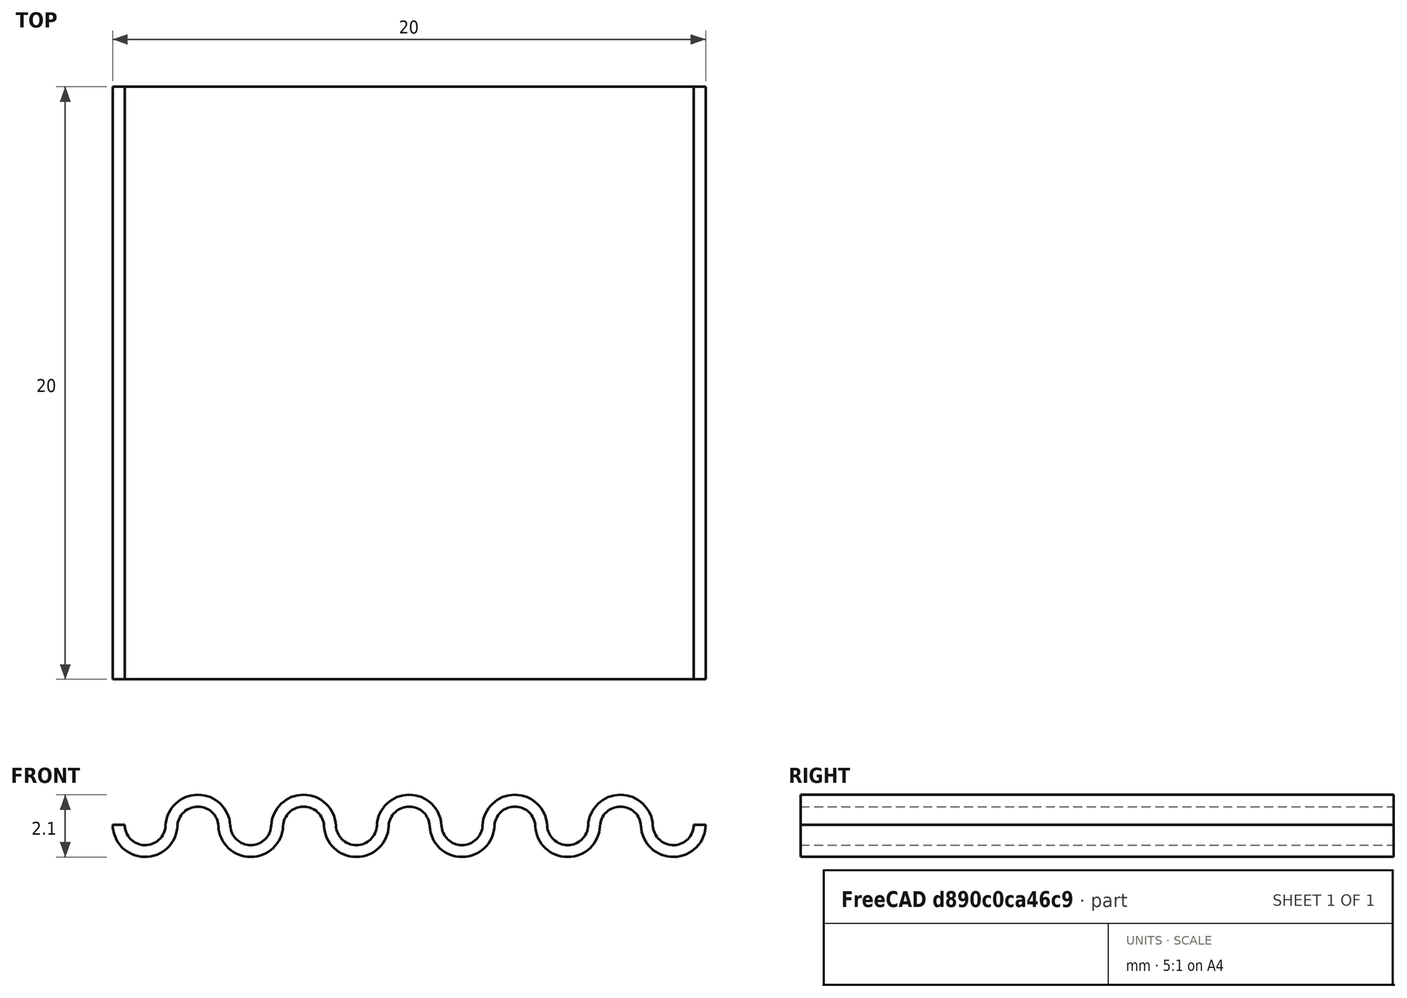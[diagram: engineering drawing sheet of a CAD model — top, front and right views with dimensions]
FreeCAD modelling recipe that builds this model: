
FCSTD DOCUMENT  (FreeCAD 1.0R39109 (Git))
Label: PLASTIC-VSN-DISPLAY-SPACER_2
License: All rights reserved
LicenseURL: https://en.wikipedia.org/wiki/All_rights_reserved
objects: Sketcher::SketchObject×1, PartDesign::Pad×1, PartDesign::Body×1
note: 6 computed .brp shape members not serialized (recipe doc carries the construction recipe); baked Part::Feature solids carry a one-line shape summary decoded from their .brp

FEATURE [Sketcher::SketchObject] Sketch
  ArcFitTolerance = 1e-06
  AttachmentSupport = -> [XZ_Plane]
  FullyConstrained = false
  MakeInternals = false
  MapMode = 5
  Placement = pos=(0,0,0) rot=(1,0,0;1.5708rad)
  sketch-geometry (27):
    g0: LineSegment [constr] StartX=-10 StartY=1.0918 StartZ=0 EndX=10 EndY=1.0918 EndZ=0
    g1: LineSegment [constr] StartX=-10 StartY=-1.0082 StartZ=0 EndX=10 EndY=-1.0082 EndZ=0
    g2: ArcOfCircle CenterX=-7.12656 CenterY=-1e-16 CenterZ=0 NormalX=0 NormalY=0 NormalZ=1 AngleXU=0 Radius=1.0918 StartAngle=0.0468888 EndAngle=3.0947
    g3: ArcOfCircle CenterX=-5.34492 CenterY=0.0836003 CenterZ=0 NormalX=0 NormalY=0 NormalZ=1 AngleXU=0 Radius=1.0918 StartAngle=3.18848 EndAngle=6.2363
    g4: ArcOfCircle CenterX=-3.56328 CenterY=0 CenterZ=0 NormalX=0 NormalY=0 NormalZ=1 AngleXU=0 Radius=1.0918 StartAngle=0.0468888 EndAngle=3.0947
    g5: ArcOfCircle CenterX=-1.78164 CenterY=0.0836003 CenterZ=0 NormalX=0 NormalY=0 NormalZ=1 AngleXU=0 Radius=1.0918 StartAngle=3.18848 EndAngle=6.2363
    g6: ArcOfCircle CenterX=0 CenterY=0 CenterZ=0 NormalX=0 NormalY=0 NormalZ=1 AngleXU=0 Radius=1.0918 StartAngle=0.0468888 EndAngle=3.0947
    g7: ArcOfCircle CenterX=1.78164 CenterY=0.0836003 CenterZ=0 NormalX=0 NormalY=0 NormalZ=1 AngleXU=0 Radius=1.0918 StartAngle=3.18848 EndAngle=6.2363
    g8: ArcOfCircle CenterX=3.56328 CenterY=-1e-16 CenterZ=0 NormalX=0 NormalY=0 NormalZ=1 AngleXU=0 Radius=1.0918 StartAngle=0.0468888 EndAngle=3.0947
    g9: ArcOfCircle CenterX=5.34492 CenterY=0.0836003 CenterZ=0 NormalX=0 NormalY=0 NormalZ=1 AngleXU=0 Radius=1.0918 StartAngle=3.18848 EndAngle=6.2363
    g10: ArcOfCircle CenterX=7.12656 CenterY=1e-16 CenterZ=0 NormalX=0 NormalY=0 NormalZ=1 AngleXU=0 Radius=1.0918 StartAngle=0.0468888 EndAngle=3.0947
    g11: ArcOfCircle CenterX=-1.78164 CenterY=0.0836003 CenterZ=0 NormalX=0 NormalY=0 NormalZ=1 AngleXU=0 Radius=0.6918 StartAngle=3.18848 EndAngle=6.2363
    g12: ArcOfCircle CenterX=-3.56328 CenterY=0 CenterZ=0 NormalX=0 NormalY=0 NormalZ=1 AngleXU=0 Radius=0.6918 StartAngle=0.0468888 EndAngle=3.0947
    g13: ArcOfCircle CenterX=-5.34492 CenterY=0.0836003 CenterZ=0 NormalX=0 NormalY=0 NormalZ=1 AngleXU=0 Radius=0.6918 StartAngle=3.18848 EndAngle=6.2363
    g14: ArcOfCircle CenterX=-7.12656 CenterY=-1e-16 CenterZ=0 NormalX=0 NormalY=0 NormalZ=1 AngleXU=0 Radius=0.6918 StartAngle=0.0468888 EndAngle=3.0947
    g15: ArcOfCircle CenterX=1.78164 CenterY=0.0836003 CenterZ=0 NormalX=0 NormalY=0 NormalZ=1 AngleXU=0 Radius=0.6918 StartAngle=3.18848 EndAngle=6.2363
    g16: ArcOfCircle CenterX=3.56328 CenterY=-1e-16 CenterZ=0 NormalX=0 NormalY=0 NormalZ=1 AngleXU=0 Radius=0.6918 StartAngle=0.0468888 EndAngle=3.0947
    g17: ArcOfCircle CenterX=5.34492 CenterY=0.0836003 CenterZ=0 NormalX=0 NormalY=0 NormalZ=1 AngleXU=0 Radius=0.6918 StartAngle=3.18848 EndAngle=6.2363
    g18: ArcOfCircle CenterX=7.12656 CenterY=1e-16 CenterZ=0 NormalX=0 NormalY=0 NormalZ=1 AngleXU=0 Radius=0.6918 StartAngle=0.0468888 EndAngle=3.0947
    g19: LineSegment [constr] StartX=1.23963e-11 StartY=0.6918 StartZ=0 EndX=-7.41186e-07 EndY=1.0918 EndZ=0
    g20: ArcOfCircle CenterX=-8.9082 CenterY=0.0836003 CenterZ=0 NormalX=0 NormalY=0 NormalZ=1 AngleXU=0 Radius=1.0918 StartAngle=3.14159 EndAngle=6.2363
    g21: ArcOfCircle CenterX=-8.9082 CenterY=0.0836003 CenterZ=0 NormalX=0 NormalY=0 NormalZ=1 AngleXU=0 Radius=0.6918 StartAngle=3.14159 EndAngle=6.2363
    g22: ArcOfCircle CenterX=8.9082 CenterY=0.0836003 CenterZ=0 NormalX=0 NormalY=0 NormalZ=1 AngleXU=0 Radius=1.0918 StartAngle=3.18848 EndAngle=6.28319
    g23: ArcOfCircle CenterX=8.9082 CenterY=0.0836003 CenterZ=0 NormalX=0 NormalY=0 NormalZ=1 AngleXU=0 Radius=0.6918 StartAngle=3.18848 EndAngle=6.28319
    g24: LineSegment StartX=9.6 StartY=0.0836003 StartZ=0 EndX=10 EndY=0.0836003 EndZ=0
    g25: LineSegment StartX=-9.6 StartY=0.0836003 StartZ=0 EndX=-10 EndY=0.0836003 EndZ=0
    g26: ArcOfCircle CenterX=0 CenterY=0 CenterZ=0 NormalX=0 NormalY=0 NormalZ=1 AngleXU=0 Radius=0.6918 StartAngle=0.0468888 EndAngle=3.0947
  constraints (72):
    c: Symmetric(g0,g0,g-2)
    c: Symmetric(g1,g1,g-2)
    c: Equal(g22,g10)
    c: Equal(g10,g9)
    c: Equal(g9,g8)
    c: Equal(g8,g7)
    c: Equal(g7,g6)
    c: Equal(g6,g5)
    c: Equal(g5,g4)
    c: Equal(g4,g3)
    c: Equal(g3,g2)
    c: Equal(g2,g20)
    c: Equal(g11,g15)
    c: Tangent(g22,g1)
    c: Tangent(g9,g1)
    c: Tangent(g7,g1)
    c: Tangent(g5,g1)
    c: Tangent(g3,g1)
    c: Tangent(g20,g1)
    c: Tangent(g2,g0)
    c: Tangent(g4,g0)
    c: Tangent(g6,g0)
    c: Tangent(g8,g0)
    c: Tangent(g10,g0)
    c: Coincident(g10,g18)
    c: Coincident(g8,g16)
    c: Coincident(g9,g17)
    c: Coincident(g7,g15)
    c: Coincident(g22,g23)
    c: Coincident(g5,g11)
    c: Coincident(g4,g12)
    c: Coincident(g3,g13)
    c: Coincident(g2,g14)
    c: Coincident(g20,g21)
    c: Coincident(g26,g6)
    c: PointOnObject(g19,g6)
    c: PointOnObject(g19,g26)
    c: Tangent(g6,g15) = 1.5708
    c: Coincident(g26,g7)
    c: Coincident(g25,g20)
    c: Coincident(g21,g25)
    c: Coincident(g9,g16)
    c: Coincident(g22,g24)
    c: Horizontal(g24)
    c: Horizontal(g24,g22)
    c: Coincident(g23,g24)
    c: Coincident(g6,g-1)
    c: DistanceY(g1,g0) = 2.1
    c: DistanceX(g1,g1) = 20
    c: DistanceY(g19,g19) = 0.4
    c: Tangent(g26,g5) = 1.5708
    c: Tangent(g11,g6) = 1.5708
    c: Tangent(g4,g11) = 1.5708
    c: Tangent(g5,g12) = 1.5708
    c: Tangent(g3,g12) = 1.5708
    c: Tangent(g4,g13) = 1.5708
    c: Tangent(g2,g13) = 1.5708
    c: Tangent(g3,g14) = 1.5708
    c: Tangent(g14,g20) = 1.5708
    c: Tangent(g21,g2) = 1.5708
    c: Horizontal(g25)
    c: Horizontal(g21,g20)
    c: Tangent(g7,g16) = 1.5708
    c: Tangent(g8,g15) = 1.5708
    c: Tangent(g9,g16,g9) = 1.5708
    c: Tangent(g17,g8) = 1.5708
    c: Tangent(g17,g10) = 1.5708
    c: Tangent(g9,g18) = 1.5708
    c: Tangent(g18,g22) = 1.5708
    c: Tangent(g23,g10) = 1.5708
    c: Vertical(g22,g0)
    c: Equal(g0,g1)
FEATURE [PartDesign::Pad] Pad
  Direction = (0,-1,2e-16)
  Length = 20
  Length2 = 10
  Midplane = true
  Placement = pos=(0,0,0) rot=(1,0,0;1.5708rad)
  Profile = -> Sketch
  ReferenceAxis = -> Sketch [N_Axis]
  Refine = true
  Suppressed = false
  Type = 0
FEATURE [PartDesign::Body] Body
  AllowCompound = false
  Group = -> [Sketch,Pad]
  Origin = -> Origin
  Tip = -> Pad
